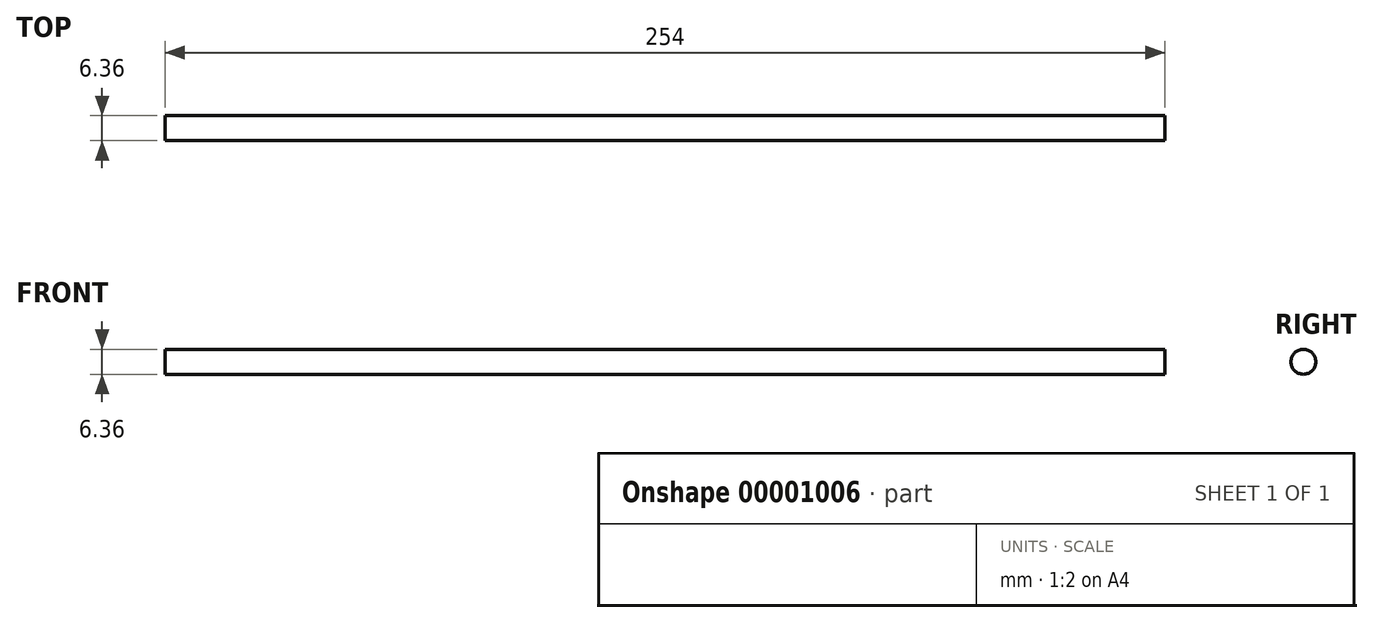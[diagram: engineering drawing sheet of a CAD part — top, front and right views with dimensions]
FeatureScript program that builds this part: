
annotation { "Feature Type Name" : "Feature", "Feature Type Description" : "" }
export const myFeature = defineFeature(function(context is Context, id is Id, definition is map)
    precondition{}
    {
        {
            var Q0;
            Q0=qCreatedBy(makeId("Right.planeOp"),FACE);
            var sketch = newSketch(context, id + "F0", { "sketchPlane" : qUnion([Q0])});
            skCircle(sketch, "E0", {"center": v(0, 0) * mm, "radius": 3.18 * mm});
            skSolve(sketch);
        }
        {
            var Q0;
            Q0=makeQuery(id+"F0.imprint","IMPRINT",FACE,{"disambiguationData":[TD([[makeQuery(id+"F0.imprint","IMPRINT",EDGE,{"derivedFrom":sQuery(id+"F0.wireOp",EDGE,"E0")}),1.0]])]});
            extrude(context, id + "F1", {"entities" : qUnion([Q0]), "endBound" : BoundingType.SYMMETRIC, "depth" : 254 * mm});
        }
    });
